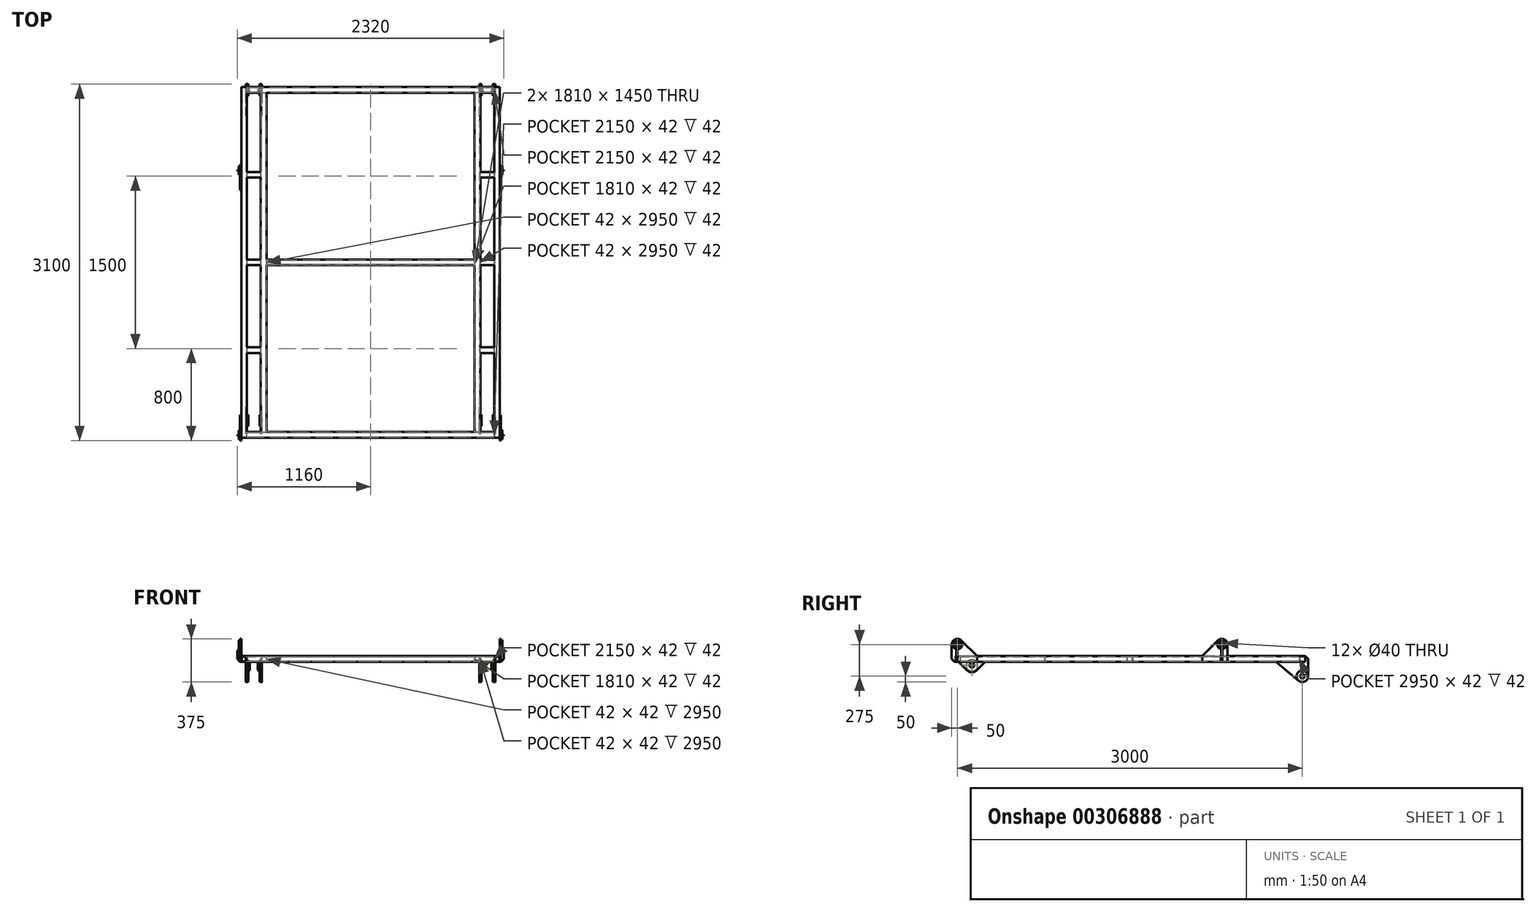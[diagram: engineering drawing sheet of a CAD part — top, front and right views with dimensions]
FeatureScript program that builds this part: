
annotation { "Feature Type Name" : "Feature", "Feature Type Description" : "" }
export const myFeature = defineFeature(function(context is Context, id is Id, definition is map)
    precondition{}
    {
        {
            assignVariable(context, id + "F0", {"name" : "width_centres", "anyValue" : 2200});
        }
        {
            assignVariable(context, id + "F1", {"name" : "offset_centres", "anyValue" : getVariable(context, 'width_centres') / 2});
        }
        {
            assignVariable(context, id + "F2", {"name" : "locater_centre_length", "anyValue" : 2300});
        }
        {
            assignVariable(context, id + "F3", {"name" : "mounting_support_offset", "anyValue" : 170});
        }
        {
            var Q0;
            Q0=qCreatedBy(makeId("Top.planeOp"),FACE);
            var sketch = newSketch(context, id + "F4", { "sketchPlane" : qUnion([Q0])});
            skLineSegment(sketch, "E0", {"start": v(0, 0) * mm, "end": v(-1100, 0) * mm, "construction": true});
            skLineSegment(sketch, "E1", {"start": v(-1100, 0) * mm, "end": v(-1100, -3050) * mm, "construction": true});
            skLineSegment(sketch, "E2", {"start": v(-1100, -3050) * mm, "end": v(0, -3050) * mm, "construction": true});
            skLineSegment(sketch, "E3", {"start": v(-1100, -1525) * mm, "end": v(0, -1525) * mm, "construction": true});
            skLineSegment(sketch, "E4", {"start": v(-930, 0) * mm, "end": v(-930, -3050) * mm, "construction": true});
            skPoint(sketch, "E5", {"position": v(-1100, 0) * mm});
            skPoint(sketch, "E6", {"position": v(-930, 0) * mm});
            skPoint(sketch, "E7", {"position": v(-1100, -1525) * mm});
            skPoint(sketch, "E8", {"position": v(-930, -1525) * mm});
            skPoint(sketch, "E9", {"position": v(-1100, -3050) * mm});
            skPoint(sketch, "E10", {"position": v(-930, -3050) * mm});
            skPoint(sketch, "E11", {"position": v(0, -3050) * mm});
            skPoint(sketch, "E12", {"position": v(0, -1525) * mm});
            skPoint(sketch, "E13", {"position": v(0, 0) * mm});
            skLineSegment(sketch, "E14", {"start": v(-930, -3050) * mm, "end": v(0, -1525) * mm, "construction": true});
            skLineSegment(sketch, "E15", {"start": v(-930, 0) * mm, "end": v(0, -1525) * mm, "construction": true});
            skSolve(sketch);
        }
        {
            var Q0;
            Q0=qCreatedBy(makeId("Front.planeOp"),FACE);
            var Q1;
            Q1=sQuery(id+"F4.wireOp",VERTEX,"E11");
            cPlane(context, id + "F5", {"entities" : qUnion([Q0, Q1]), "cplaneType" : CPlaneType.PLANE_POINT, "offset" : 25 * mm, "width" : 150 * mm, "height" : 150 * mm});
        }
        {
            var Q0;
            Q0=qCreatedBy(id+"F5.planeOp",FACE);
            var sketch = newSketch(context, id + "F6", { "sketchPlane" : qUnion([Q0])});
            skPoint(sketch, "E16", {"position": v(-1203.55, -13.4) * mm});
            skPoint(sketch, "E17", {"position": v(-1303.55, -13.4) * mm});
            skPoint(sketch, "E18", {"position": v(-1003.55, -13.4) * mm});
            skLineSegment(sketch, "E19.bottom", {"start": v(-1125, 25) * mm, "end": v(-1075, 25) * mm});
            skLineSegment(sketch, "E19.top", {"start": v(-1125, -25) * mm, "end": v(-1075, -25) * mm});
            skLineSegment(sketch, "E19.left", {"start": v(-1125, 25) * mm, "end": v(-1125, -25) * mm});
            skLineSegment(sketch, "E19.right", {"start": v(-1075, 25) * mm, "end": v(-1075, -25) * mm});
            skPoint(sketch, "E19.middle", {"position": v(-1100, 0) * mm});
            skLineSegment(sketch, "E20.0", {"start": v(-1121, 21) * mm, "end": v(-1079, 21) * mm});
            skLineSegment(sketch, "E20.1", {"start": v(-1121, 21) * mm, "end": v(-1121, -21) * mm});
            skLineSegment(sketch, "E20.2", {"start": v(-1121, -21) * mm, "end": v(-1079, -21) * mm});
            skLineSegment(sketch, "E20.3", {"start": v(-1079, 21) * mm, "end": v(-1079, -21) * mm});
            skPoint(sketch, "E21", {"position": v(-1125, 25) * mm});
            skPoint(sketch, "E22", {"position": v(-1075, 25) * mm});
            skPoint(sketch, "E23", {"position": v(-1075, -25) * mm});
            skPoint(sketch, "E24", {"position": v(-1125, -25) * mm});
            skSolve(sketch);
        }
        {
            var Q0;
            Q0 = qSketchRegion(id + "F6", true);
            var Q1;
            Q1=sQuery(id+"F4.wireOp",VERTEX,"E5");
            extrude(context, id + "F7", {"entities" : qUnion([Q0]), "endBound" : BoundingType.UP_TO_VERTEX, "oppositeDirection" : true, "endBoundEntityVertex" : qUnion([Q1]), "depth" : 25 * mm});
        }
        {
            var Q0;
            Q0=qCreatedBy(makeId("Right.planeOp"),FACE);
            var sketch = newSketch(context, id + "F8", { "sketchPlane" : qUnion([Q0])});
            skPoint(sketch, "E25", {"position": v(-1835.18, -71.7) * mm});
            skPoint(sketch, "E26", {"position": v(-1935.18, -71.7) * mm});
            skPoint(sketch, "E27", {"position": v(-1635.18, -71.7) * mm});
            skLineSegment(sketch, "E28.bottom", {"start": v(-3050, 25) * mm, "end": v(-3000, 25) * mm});
            skLineSegment(sketch, "E28.top", {"start": v(-3050, -25) * mm, "end": v(-3000, -25) * mm});
            skLineSegment(sketch, "E28.left", {"start": v(-3050, 25) * mm, "end": v(-3050, -25) * mm});
            skLineSegment(sketch, "E28.right", {"start": v(-3000, 25) * mm, "end": v(-3000, -25) * mm});
            skPoint(sketch, "E28.middle", {"position": v(-3025, 0) * mm});
            skLineSegment(sketch, "E29.0", {"start": v(-3046, 21) * mm, "end": v(-3004, 21) * mm});
            skLineSegment(sketch, "E29.1", {"start": v(-3046, 21) * mm, "end": v(-3046, -21) * mm});
            skLineSegment(sketch, "E29.2", {"start": v(-3046, -21) * mm, "end": v(-3004, -21) * mm});
            skLineSegment(sketch, "E29.3", {"start": v(-3004, 21) * mm, "end": v(-3004, -21) * mm});
            skPoint(sketch, "E30", {"position": v(-3050, 25) * mm});
            skPoint(sketch, "E31", {"position": v(-3000, 25) * mm});
            skPoint(sketch, "E32", {"position": v(-3000, -25) * mm});
            skPoint(sketch, "E33", {"position": v(-3050, -25) * mm});
            skPoint(sketch, "E34", {"position": v(-210.58, -52.8) * mm});
            skPoint(sketch, "E35", {"position": v(-310.58, -52.8) * mm});
            skPoint(sketch, "E36", {"position": v(-10.58, -52.8) * mm});
            skLineSegment(sketch, "E37.bottom", {"start": v(-50, 25) * mm, "end": v(0, 25) * mm});
            skLineSegment(sketch, "E37.top", {"start": v(-50, -25) * mm, "end": v(0, -25) * mm});
            skLineSegment(sketch, "E37.left", {"start": v(-50, 25) * mm, "end": v(-50, -25) * mm});
            skLineSegment(sketch, "E37.right", {"start": v(0, 25) * mm, "end": v(0, -25) * mm});
            skPoint(sketch, "E37.middle", {"position": v(-25, 0) * mm});
            skLineSegment(sketch, "E38.0", {"start": v(-46, 21) * mm, "end": v(-4, 21) * mm});
            skLineSegment(sketch, "E38.1", {"start": v(-46, 21) * mm, "end": v(-46, -21) * mm});
            skLineSegment(sketch, "E38.2", {"start": v(-46, -21) * mm, "end": v(-4, -21) * mm});
            skLineSegment(sketch, "E38.3", {"start": v(-4, 21) * mm, "end": v(-4, -21) * mm});
            skPoint(sketch, "E39", {"position": v(-50, 25) * mm});
            skPoint(sketch, "E40", {"position": v(0, 25) * mm});
            skPoint(sketch, "E41", {"position": v(0, -25) * mm});
            skPoint(sketch, "E42", {"position": v(-50, -25) * mm});
            skSolve(sketch);
        }
        {
            var Q0;
            Q0 = qSketchRegion(id + "F8", true);
            var Q1;
            Q1=makeQuery(id+"F7.opExtrude","SWEPT_BODY",BODY,{"disambiguationData":[OSD([sQuery(id+"F6.wireOp",EDGE,"E19.bottom"),sQuery(id+"F6.wireOp",EDGE,"E19.top"),sQuery(id+"F6.wireOp",EDGE,"E19.left"),sQuery(id+"F6.wireOp",EDGE,"E19.right"),sQuery(id+"F6.wireOp",EDGE,"E20.0"),sQuery(id+"F6.wireOp",EDGE,"E20.1"),sQuery(id+"F6.wireOp",EDGE,"E20.2"),sQuery(id+"F6.wireOp",EDGE,"E20.3")])]});
            extrude(context, id + "F9", {"entities" : qUnion([Q0]), "operationType" : NewBodyOperationType.ADD, "endBound" : BoundingType.UP_TO_NEXT, "oppositeDirection" : true, "endBoundEntityBody" : qUnion([Q1]), "depth" : 25 * mm});
        }
        {
            var Q0;
            Q0=qCreatedBy(makeId("Front.planeOp"),FACE);
            var Q1;
            Q1=sQuery(id+"F4.wireOp",VERTEX,"E12");
            cPlane(context, id + "F10", {"entities" : qUnion([Q0, Q1]), "cplaneType" : CPlaneType.PLANE_POINT, "offset" : 25 * mm, "width" : 150 * mm, "height" : 150 * mm});
        }
        {
            var Q0;
            Q0=qCreatedBy(id+"F10.planeOp",FACE);
            var sketch = newSketch(context, id + "F11", { "sketchPlane" : qUnion([Q0])});
            skPoint(sketch, "E43", {"position": v(-1051.26, -74.87) * mm});
            skPoint(sketch, "E44", {"position": v(-1151.26, -74.87) * mm});
            skPoint(sketch, "E45", {"position": v(-851.26, -74.87) * mm});
            skLineSegment(sketch, "E46.bottom", {"start": v(-955, 25) * mm, "end": v(-905, 25) * mm});
            skLineSegment(sketch, "E46.top", {"start": v(-955, -25) * mm, "end": v(-905, -25) * mm});
            skLineSegment(sketch, "E46.left", {"start": v(-955, 25) * mm, "end": v(-955, -25) * mm});
            skLineSegment(sketch, "E46.right", {"start": v(-905, 25) * mm, "end": v(-905, -25) * mm});
            skPoint(sketch, "E46.middle", {"position": v(-930, 0) * mm});
            skLineSegment(sketch, "E47.0", {"start": v(-951, 21) * mm, "end": v(-909, 21) * mm});
            skLineSegment(sketch, "E47.1", {"start": v(-951, 21) * mm, "end": v(-951, -21) * mm});
            skLineSegment(sketch, "E47.2", {"start": v(-951, -21) * mm, "end": v(-909, -21) * mm});
            skLineSegment(sketch, "E47.3", {"start": v(-909, 21) * mm, "end": v(-909, -21) * mm});
            skPoint(sketch, "E48", {"position": v(-955, 25) * mm});
            skPoint(sketch, "E49", {"position": v(-905, 25) * mm});
            skPoint(sketch, "E50", {"position": v(-905, -25) * mm});
            skPoint(sketch, "E51", {"position": v(-955, -25) * mm});
            skSolve(sketch);
        }
        {
            var Q0;
            Q0 = qSketchRegion(id + "F11", true);
            extrude(context, id + "F12", {"entities" : qUnion([Q0]), "operationType" : NewBodyOperationType.ADD, "depth" : (getVariable(context, 'locater_centre_length') + 700 - 50) * mm, "symmetric" : true});
        }
        {
            var Q0;
            Q0=qCreatedBy(makeId("Right.planeOp"),FACE);
            var sketch = newSketch(context, id + "F13", { "sketchPlane" : qUnion([Q0])});
            skPoint(sketch, "E52", {"position": v(-973.87, -66.92) * mm});
            skPoint(sketch, "E53", {"position": v(-1073.87, -66.92) * mm});
            skPoint(sketch, "E54", {"position": v(-773.87, -66.92) * mm});
            skLineSegment(sketch, "E55.bottom", {"start": v(-1550, 25) * mm, "end": v(-1500, 25) * mm});
            skLineSegment(sketch, "E55.top", {"start": v(-1550, -25) * mm, "end": v(-1500, -25) * mm});
            skLineSegment(sketch, "E55.left", {"start": v(-1550, 25) * mm, "end": v(-1550, -25) * mm});
            skLineSegment(sketch, "E55.right", {"start": v(-1500, 25) * mm, "end": v(-1500, -25) * mm});
            skPoint(sketch, "E55.middle", {"position": v(-1525, 0) * mm});
            skLineSegment(sketch, "E56.0", {"start": v(-1546, 21) * mm, "end": v(-1504, 21) * mm});
            skLineSegment(sketch, "E56.1", {"start": v(-1546, 21) * mm, "end": v(-1546, -21) * mm});
            skLineSegment(sketch, "E56.2", {"start": v(-1546, -21) * mm, "end": v(-1504, -21) * mm});
            skLineSegment(sketch, "E56.3", {"start": v(-1504, 21) * mm, "end": v(-1504, -21) * mm});
            skPoint(sketch, "E57", {"position": v(-1550, 25) * mm});
            skPoint(sketch, "E58", {"position": v(-1500, 25) * mm});
            skPoint(sketch, "E59", {"position": v(-1500, -25) * mm});
            skPoint(sketch, "E60", {"position": v(-1550, -25) * mm});
            skSolve(sketch);
        }
        {
            var Q0;
            Q0 = qSketchRegion(id + "F13", true);
            var Q1;
            Q1=makeQuery(id+"F7.opExtrude","SWEPT_BODY",BODY,{"disambiguationData":[OSD([sQuery(id+"F6.wireOp",EDGE,"E19.bottom"),sQuery(id+"F6.wireOp",EDGE,"E19.top"),sQuery(id+"F6.wireOp",EDGE,"E19.left"),sQuery(id+"F6.wireOp",EDGE,"E19.right"),sQuery(id+"F6.wireOp",EDGE,"E20.0"),sQuery(id+"F6.wireOp",EDGE,"E20.1"),sQuery(id+"F6.wireOp",EDGE,"E20.2"),sQuery(id+"F6.wireOp",EDGE,"E20.3")])]});
            extrude(context, id + "F14", {"entities" : qUnion([Q0]), "operationType" : NewBodyOperationType.ADD, "endBound" : BoundingType.UP_TO_BODY, "oppositeDirection" : true, "endBoundEntityBody" : qUnion([Q1]), "depth" : 25 * mm});
        }
        {
            var Q0;
            Q0=qCreatedBy(makeId("Right.planeOp"),FACE);
            cPlane(context, id + "F15", {"entities" : qUnion([Q0]), "cplaneType" : CPlaneType.OFFSET, "offset" : (getVariable(context, 'offset_centres') + 25) * mm, "oppositeDirection" : true, "width" : 150 * mm, "height" : 150 * mm});
        }
        {
            var Q0;
            Q0=qCreatedBy(id+"F15.planeOp",FACE);
            var sketch = newSketch(context, id + "F16", { "sketchPlane" : qUnion([Q0])});
            skPoint(sketch, "E61.0", {"position": v(-3050, -25) * mm});
            skPoint(sketch, "E62", {"position": v(-3025, 125) * mm});
            skArc(sketch, "E63", {"start": v(-2989.64, 160.36) * mm, "mid": v(-3044.13, 171.2) * mm, "end": v(-3075, 125) * mm});
            skLineSegment(sketch, "E64", {"start": v(-3050, -25) * mm, "end": v(-3075, 0) * mm});
            skLineSegment(sketch, "E65", {"start": v(-3075, 125) * mm, "end": v(-3075, 0) * mm});
            skPoint(sketch, "E66.0", {"position": v(-3050, 25) * mm});
            skLineSegment(sketch, "E67.0", {"start": v(-2854.29, 25) * mm, "end": v(-1550, 25) * mm, "construction": true});
            skLineSegment(sketch, "E68", {"start": v(-2989.64, 160.36) * mm, "end": v(-2854.29, 25) * mm});
            skCircle(sketch, "E69", {"center": v(-3025, 125) * mm, "radius": 20 * mm});
            skLineSegment(sketch, "E70", {"start": v(-2854.29, 25) * mm, "end": v(-2854.29, -25) * mm});
            skLineSegment(sketch, "E71", {"start": v(-2854.29, -25) * mm, "end": v(-3050, -25) * mm});
            skPoint(sketch, "E72.orphan", {"position": v(-3000, 25) * mm});
            skSolve(sketch);
        }
        {
            var Q0;
            Q0 = qSketchRegion(id + "F16", true);
            extrude(context, id + "F17", {"entities" : qUnion([Q0]), "operationType" : NewBodyOperationType.ADD, "oppositeDirection" : true, "depth" : 10 * mm});
        }
        {
            var Q0;
            Q0=qCreatedBy(id+"F15.planeOp",FACE);
            var sketch = newSketch(context, id + "F18", { "sketchPlane" : qUnion([Q0])});
            skCircle(sketch, "E73", {"center": v(-725, 125) * mm, "radius": 20 * mm});
            skArc(sketch, "E74", {"start": v(-689.64, 160.36) * mm, "mid": v(-725, 175) * mm, "end": v(-760.36, 160.36) * mm});
            skLineSegment(sketch, "E75.0", {"start": v(-1500, 25) * mm, "end": v(-895.71, 25) * mm, "construction": true});
            skLineSegment(sketch, "E76", {"start": v(-895.71, 25) * mm, "end": v(-675, 25) * mm});
            skLineSegment(sketch, "E77", {"start": v(-895.71, 25) * mm, "end": v(-760.36, 160.36) * mm});
            skLineSegment(sketch, "E78.0", {"start": v(-1500, -25) * mm, "end": v(-675, -25) * mm, "construction": true});
            skLineSegment(sketch, "E79", {"start": v(-895.71, 25) * mm, "end": v(-895.71, -25) * mm});
            skLineSegment(sketch, "E80", {"start": v(-895.71, -25) * mm, "end": v(-675, -25) * mm});
            skLineSegment(sketch, "E81.trimOffspring", {"start": v(-282.87, 25) * mm, "end": v(-50, 25) * mm, "construction": true});
            skArc(sketch, "E82", {"start": v(-689.64, 160.36) * mm, "mid": v(-678.8, 144.13) * mm, "end": v(-675, 125) * mm});
            skLineSegment(sketch, "E83", {"start": v(-675, 125) * mm, "end": v(-675, -25) * mm});
            skPoint(sketch, "E84.orphan", {"position": v(-689.64, 89.64) * mm});
            skLineSegment(sketch, "E85.trimOffspring", {"start": v(-282.87, -25) * mm, "end": v(-50, -25) * mm, "construction": true});
            skCircle(sketch, "E86.0", {"center": v(-3025, 125) * mm, "radius": 20 * mm, "construction": true});
            skSolve(sketch);
        }
        {
            var Q0;
            Q0 = qSketchRegion(id + "F18", true);
            extrude(context, id + "F19", {"entities" : qUnion([Q0]), "operationType" : NewBodyOperationType.ADD, "oppositeDirection" : true, "depth" : 10 * mm});
        }
        {
            var Q0;
            Q0=qCreatedBy(id+"F15.planeOp",FACE);
            cPlane(context, id + "F20", {"entities" : qUnion([Q0]), "cplaneType" : CPlaneType.OFFSET, "offset" : 50 * mm, "width" : 150 * mm, "height" : 150 * mm});
        }
        {
            var Q0;
            Q0=qCreatedBy(id+"F20.planeOp",FACE);
            var sketch = newSketch(context, id + "F21", { "sketchPlane" : qUnion([Q0])});
            skPoint(sketch, "E87", {"position": v(-25, -150) * mm});
            skCircle(sketch, "E88", {"center": v(-25, -150) * mm, "radius": 20 * mm});
            skArc(sketch, "E89", {"start": v(-56.96, -188.45) * mm, "mid": v(-3.77, -195.27) * mm, "end": v(25, -150) * mm});
            skLineSegment(sketch, "E90.0", {"start": v(-1500, -25) * mm, "end": v(-50, -25) * mm, "construction": true});
            skPoint(sketch, "E91.0", {"position": v(0, -25) * mm});
            skPoint(sketch, "E92.0", {"position": v(0, 25) * mm});
            skLineSegment(sketch, "E93", {"start": v(0, 25) * mm, "end": v(25, 0) * mm});
            skLineSegment(sketch, "E94", {"start": v(25, -150) * mm, "end": v(25, 0) * mm});
            skLineSegment(sketch, "E95", {"start": v(-56.96, -188.45) * mm, "end": v(-253.57, -25) * mm});
            skLineSegment(sketch, "E96", {"start": v(-253.57, -25) * mm, "end": v(0, -25) * mm});
            skLineSegment(sketch, "E97", {"start": v(0, 25) * mm, "end": v(0, -25) * mm});
            skPoint(sketch, "E98.end.orphan", {"position": v(-253.57, 25) * mm});
            skSolve(sketch);
        }
        {
            var Q0;
            Q0 = qSketchRegion(id + "F21", true);
            extrude(context, id + "F22", {"entities" : qUnion([Q0]), "operationType" : NewBodyOperationType.ADD, "oppositeDirection" : true, "depth" : 10 * mm});
        }
        {
            var Q0;
            Q0=qCreatedBy(id+"F20.planeOp",FACE);
            var sketch = newSketch(context, id + "F23", { "sketchPlane" : qUnion([Q0])});
            skPoint(sketch, "E99", {"position": v(-2900, -55) * mm});
            skPoint(sketch, "E100.0", {"position": v(-3050, -25) * mm});
            skLineSegment(sketch, "E101.0", {"start": v(-3000, 25) * mm, "end": v(-1550, 25) * mm, "construction": true});
            skLineSegment(sketch, "E102.0", {"start": v(-3000, -25) * mm, "end": v(-1550, -25) * mm, "construction": true});
            skPoint(sketch, "E103.0", {"position": v(-3000, 0) * mm});
            skCircle(sketch, "E104", {"center": v(-2900, -55) * mm, "radius": 20 * mm});
            skArc(sketch, "E105", {"start": v(-2942.43, -97.43) * mm, "mid": v(-2900, -115) * mm, "end": v(-2857.57, -97.43) * mm});
            skLineSegment(sketch, "E106", {"start": v(-2942.43, -97.43) * mm, "end": v(-3014.85, -25) * mm});
            skLineSegment(sketch, "E107", {"start": v(-2857.57, -97.43) * mm, "end": v(-2785.15, -25) * mm});
            skLineSegment(sketch, "E108", {"start": v(-3000, -25) * mm, "end": v(-2785.15, -25) * mm});
            skLineSegment(sketch, "E109", {"start": v(-3014.85, -25) * mm, "end": v(-3000, -25) * mm});
            skSolve(sketch);
        }
        {
            var Q0;
            Q0 = qSketchRegion(id + "F23", true);
            extrude(context, id + "F24", {"entities" : qUnion([Q0]), "operationType" : NewBodyOperationType.ADD, "oppositeDirection" : true, "depth" : 10 * mm});
        }
        {
            var Q0;
            Q0=qCreatedBy(id+"F20.planeOp",FACE);
            cPlane(context, id + "F25", {"entities" : qUnion([Q0]), "cplaneType" : CPlaneType.OFFSET, "offset" : (getVariable(context, 'mounting_support_offset') - 50) * mm, "width" : 150 * mm, "height" : 150 * mm});
        }
        {
            var Q0;
            Q0=qCreatedBy(id+"F25.planeOp",FACE);
            var sketch = newSketch(context, id + "F26", { "sketchPlane" : qUnion([Q0])});
            skLineSegment(sketch, "E110.0", {"start": v(-56.96, -188.45) * mm, "end": v(-253.57, -25) * mm});
            skPoint(sketch, "E111.0", {"position": v(-3.77, -195.27) * mm});
            skArc(sketch, "E112.0", {"start": v(-56.96, -188.45) * mm, "mid": v(-3.77, -195.27) * mm, "end": v(25, -150) * mm});
            skLineSegment(sketch, "E113.0", {"start": v(25, -150) * mm, "end": v(25, 0) * mm});
            skLineSegment(sketch, "E114.0", {"start": v(0, 25) * mm, "end": v(25, 0) * mm});
            skPoint(sketch, "E115.0", {"position": v(0, -25) * mm});
            skLineSegment(sketch, "E116", {"start": v(-253.57, -25) * mm, "end": v(0, -25) * mm});
            skLineSegment(sketch, "E117", {"start": v(0, -25) * mm, "end": v(0, 25) * mm});
            skCircle(sketch, "E118.0", {"center": v(-25, -150) * mm, "radius": 20 * mm});
            skCircle(sketch, "E119.0", {"center": v(-2900, -55) * mm, "radius": 20 * mm});
            skLineSegment(sketch, "E120.0", {"start": v(-2857.57, -97.43) * mm, "end": v(-2785.15, -25) * mm});
            skArc(sketch, "E121.0", {"start": v(-2942.43, -97.43) * mm, "mid": v(-2900, -115) * mm, "end": v(-2857.57, -97.43) * mm});
            skLineSegment(sketch, "E122.0", {"start": v(-2942.43, -97.43) * mm, "end": v(-3014.85, -25) * mm});
            skLineSegment(sketch, "E123", {"start": v(-3014.85, -25) * mm, "end": v(-2785.15, -25) * mm});
            skSolve(sketch);
        }
        {
            var Q0;
            Q0 = qSketchRegion(id + "F26", true);
            extrude(context, id + "F27", {"entities" : qUnion([Q0]), "operationType" : NewBodyOperationType.ADD, "depth" : 10 * mm});
        }
        {
            var Q0;
            Q0=qCreatedBy(id+"F15.planeOp",FACE);
            cPlane(context, id + "F28", {"entities" : qUnion([Q0]), "cplaneType" : CPlaneType.OFFSET, "offset" : 10 * mm, "oppositeDirection" : true, "width" : 150 * mm, "height" : 150 * mm});
        }
        {
            var Q0;
            Q0=qCreatedBy(id+"F28.planeOp",FACE);
            var sketch = newSketch(context, id + "F29", { "sketchPlane" : qUnion([Q0])});
            skCircle(sketch, "E124.0", {"center": v(-725, 125) * mm, "radius": 20 * mm});
            skCircle(sketch, "E125", {"center": v(-725, 125) * mm, "radius": 40 * mm});
            skCircle(sketch, "E126.0", {"center": v(-3025, 125) * mm, "radius": 20 * mm});
            skCircle(sketch, "E127", {"center": v(-3025, 125) * mm, "radius": 40 * mm});
            skSolve(sketch);
        }
        {
            var Q0;
            Q0 = qSketchRegion(id + "F29", true);
            extrude(context, id + "F30", {"entities" : qUnion([Q0]), "operationType" : NewBodyOperationType.ADD, "oppositeDirection" : true, "depth" : 10 * mm});
        }
        {
            var Q0;
            Q0=qCreatedBy(id+"F20.planeOp",FACE);
            var sketch = newSketch(context, id + "F31", { "sketchPlane" : qUnion([Q0])});
            skCircle(sketch, "E128.0", {"center": v(-2900, -55) * mm, "radius": 20 * mm});
            skCircle(sketch, "E129", {"center": v(-2900, -55) * mm, "radius": 50 * mm});
            skCircle(sketch, "E130.0", {"center": v(-25, -150) * mm, "radius": 20 * mm});
            skCircle(sketch, "E131", {"center": v(-25, -150) * mm, "radius": 50 * mm});
            skSolve(sketch);
        }
        {
            var Q0;
            Q0 = qSketchRegion(id + "F31", true);
            extrude(context, id + "F32", {"entities" : qUnion([Q0]), "operationType" : NewBodyOperationType.ADD, "depth" : 10 * mm});
        }
        {
            var Q0;
            Q0=qCreatedBy(id+"F25.planeOp",FACE);
            var sketch = newSketch(context, id + "F33", { "sketchPlane" : qUnion([Q0])});
            skCircle(sketch, "E132.0", {"center": v(-2900, -55) * mm, "radius": 50 * mm});
            skCircle(sketch, "E133.0", {"center": v(-2900, -55) * mm, "radius": 20 * mm});
            skCircle(sketch, "E134.0.0", {"center": v(-25, -150) * mm, "radius": 50 * mm});
            skCircle(sketch, "E135.0", {"center": v(-25, -150) * mm, "radius": 20 * mm});
            skSolve(sketch);
        }
        {
            var Q0;
            Q0 = qSketchRegion(id + "F33", true);
            extrude(context, id + "F34", {"entities" : qUnion([Q0]), "operationType" : NewBodyOperationType.ADD, "oppositeDirection" : true, "depth" : 10 * mm});
        }
        {
            var Q0;
            Q0=qCreatedBy(id+"F5.planeOp",FACE);
            cPlane(context, id + "F35", {"entities" : qUnion([Q0]), "cplaneType" : CPlaneType.OFFSET, "offset" : 25 * mm, "oppositeDirection" : true, "width" : 150 * mm, "height" : 150 * mm});
        }
        {
            var Q0;
            Q0=qCreatedBy(id+"F35.planeOp",FACE);
            var sketch = newSketch(context, id + "F36", { "sketchPlane" : qUnion([Q0])});
            skPoint(sketch, "E136.0", {"position": v(-1135, -25) * mm});
            skLineSegment(sketch, "E137", {"start": v(-1135, -25) * mm, "end": v(-1135, 84.9) * mm});
            skLineSegment(sketch, "E138", {"start": v(-1145, 84.9) * mm, "end": v(-1160, 69.9) * mm});
            skLineSegment(sketch, "E139", {"start": v(-1160, 69.9) * mm, "end": v(-1160, 0) * mm});
            skLineSegment(sketch, "E140", {"start": v(-1160, 0) * mm, "end": v(-1135, -25) * mm});
            skLineSegment(sketch, "E141", {"start": v(-1145, 84.9) * mm, "end": v(-1135, 84.9) * mm});
            skPoint(sketch, "E142.orphan", {"position": v(-1135, 85) * mm});
            skSolve(sketch);
        }
        {
            var Q0;
            Q0 = qSketchRegion(id + "F36", true);
            extrude(context, id + "F37", {"entities" : qUnion([Q0]), "operationType" : NewBodyOperationType.ADD, "depth" : 10 * mm});
        }
        {
            var Q0;
            Q0=qCreatedBy(id+"F35.planeOp",FACE);
            cPlane(context, id + "F38", {"entities" : qUnion([Q0]), "cplaneType" : CPlaneType.OFFSET, "offset" : (getVariable(context, 'locater_centre_length')) * mm, "oppositeDirection" : true, "width" : 150 * mm, "height" : 150 * mm});
        }
        {
            var Q0;
            Q0=qCreatedBy(id+"F38.planeOp",FACE);
            var sketch = newSketch(context, id + "F39", { "sketchPlane" : qUnion([Q0])});
            skLineSegment(sketch, "E143.0.0", {"start": v(-1160, 69.9) * mm, "end": v(-1145, 84.9) * mm});
            skLineSegment(sketch, "E143.0.1", {"start": v(-1145, 84.9) * mm, "end": v(-1135, 84.9) * mm});
            skLineSegment(sketch, "E143.0.2", {"start": v(-1135, 84.9) * mm, "end": v(-1135, -25) * mm});
            skLineSegment(sketch, "E143.0.3", {"start": v(-1135, -25) * mm, "end": v(-1160, 0) * mm});
            skLineSegment(sketch, "E143.0.4", {"start": v(-1160, 0) * mm, "end": v(-1160, 69.9) * mm});
            skSolve(sketch);
        }
        {
            var Q0;
            Q0 = qSketchRegion(id + "F39", true);
            extrude(context, id + "F40", {"entities" : qUnion([Q0]), "operationType" : NewBodyOperationType.ADD, "depth" : 10 * mm, "symmetric" : true});
        }
        {
            var Q0;
            Q0=qCreatedBy(makeId("Front.planeOp"),FACE);
            cPlane(context, id + "F41", {"entities" : qUnion([Q0]), "cplaneType" : CPlaneType.OFFSET, "offset" : 25 * mm, "width" : 150 * mm, "height" : 150 * mm});
        }
        {
            var Q0;
            Q0=qCreatedBy(id+"F41.planeOp",FACE);
            var sketch = newSketch(context, id + "F42", { "sketchPlane" : qUnion([Q0])});
            skLineSegment(sketch, "E144.0", {"start": v(-1075, -25) * mm, "end": v(-955, -25) * mm, "construction": true});
            skLineSegment(sketch, "E145", {"start": v(-955, -109.9) * mm, "end": v(-955, -25) * mm});
            skLineSegment(sketch, "E146", {"start": v(-955, -25) * mm, "end": v(-980, -25) * mm});
            skLineSegment(sketch, "E147", {"start": v(-980, -25) * mm, "end": v(-980, -95) * mm});
            skLineSegment(sketch, "E148", {"start": v(-980, -95) * mm, "end": v(-965.1, -109.9) * mm});
            skLineSegment(sketch, "E149", {"start": v(-1075, -109.9) * mm, "end": v(-1075, -25) * mm});
            skLineSegment(sketch, "E150", {"start": v(-1075, -25) * mm, "end": v(-1050, -25) * mm});
            skLineSegment(sketch, "E151", {"start": v(-1050, -25) * mm, "end": v(-1050, -95) * mm});
            skLineSegment(sketch, "E152", {"start": v(-1050, -95) * mm, "end": v(-1064.9, -109.9) * mm});
            skLineSegment(sketch, "E153", {"start": v(-955, -109.9) * mm, "end": v(-965.1, -109.9) * mm});
            skLineSegment(sketch, "E154", {"start": v(-1064.9, -109.9) * mm, "end": v(-1075, -109.9) * mm});
            skSolve(sketch);
        }
        {
            var Q0;
            Q0 = qSketchRegion(id + "F42", true);
            extrude(context, id + "F43", {"entities" : qUnion([Q0]), "operationType" : NewBodyOperationType.ADD, "depth" : 10 * mm, "symmetric" : true});
        }
        {
            var Q0;
            Q0=qCreatedBy(makeId("Right.planeOp"),FACE);
            var sketch = newSketch(context, id + "F44", { "sketchPlane" : qUnion([Q0])});
            skCircle(sketch, "E155.0", {"center": v(-3025, 125) * mm, "radius": 20 * mm, "construction": true});
            skCircle(sketch, "E156.0", {"center": v(-2900, -55) * mm, "radius": 20 * mm, "construction": true});
            skCircle(sketch, "E157.0", {"center": v(-725, 125) * mm, "radius": 20 * mm, "construction": true});
            skCircle(sketch, "E158.0", {"center": v(-25, -150) * mm, "radius": 20 * mm, "construction": true});
            skLineSegment(sketch, "E159", {"start": v(-3025, 125) * mm, "end": v(-725, 125) * mm, "construction": true});
            skLineSegment(sketch, "E160", {"start": v(-2900, -55) * mm, "end": v(-2900, 125) * mm, "construction": true});
            skLineSegment(sketch, "E161", {"start": v(-725, 125) * mm, "end": v(-725, 0) * mm, "construction": true});
            skLineSegment(sketch, "E162", {"start": v(-25, -150) * mm, "end": v(-25, 0) * mm, "construction": true});
            skPoint(sketch, "E163.0", {"position": v(-3025, -21) * mm});
            skPoint(sketch, "E164.0", {"position": v(-3050, 0) * mm});
            skPoint(sketch, "E165", {"position": v(-3025, 0) * mm});
            skPoint(sketch, "E166", {"position": v(-25, 0) * mm});
            skSolve(sketch);
        }
        {
            var Q0;
            Q0=qCreatedBy(id+"F25.planeOp",FACE);
            var sketch = newSketch(context, id + "F45", { "sketchPlane" : qUnion([Q0])});
            skPoint(sketch, "E167.0", {"position": v(-1525, 0) * mm});
            skLineSegment(sketch, "E168.0", {"start": v(-725, 125) * mm, "end": v(-725, 0) * mm, "construction": true});
            skPoint(sketch, "E169.0", {"position": v(-2287.5, 0) * mm});
            skPoint(sketch, "E170.0", {"position": v(-762.5, 0) * mm});
            skLineSegment(sketch, "E171.bottom", {"start": v(-2312.5, 25) * mm, "end": v(-2262.5, 25) * mm});
            skLineSegment(sketch, "E171.top", {"start": v(-2266.5, -25) * mm, "end": v(-2262.5, -25) * mm});
            skLineSegment(sketch, "E171.left", {"start": v(-2312.5, 25) * mm, "end": v(-2312.5, 21) * mm});
            skLineSegment(sketch, "E171.right", {"start": v(-2262.5, 25) * mm, "end": v(-2262.5, -25) * mm});
            skLineSegment(sketch, "E172.0", {"start": v(-2266.5, 21) * mm, "end": v(-2266.5, -25) * mm});
            skLineSegment(sketch, "E172.1", {"start": v(-2312.5, 21) * mm, "end": v(-2266.5, 21) * mm});
            skPoint(sketch, "E173.orphan", {"position": v(-2312.5, -25) * mm});
            skPoint(sketch, "E174", {"position": v(-2262.5, 25) * mm});
            skPoint(sketch, "E175", {"position": v(-2312.5, 25) * mm});
            skPoint(sketch, "E176", {"position": v(-2262.5, -25) * mm});
            skLineSegment(sketch, "E177.bottom", {"start": v(-1550, 25) * mm, "end": v(-1500, 25) * mm});
            skLineSegment(sketch, "E177.top", {"start": v(-1504, -25) * mm, "end": v(-1500, -25) * mm});
            skLineSegment(sketch, "E177.left", {"start": v(-1550, 25) * mm, "end": v(-1550, 21) * mm});
            skLineSegment(sketch, "E177.right", {"start": v(-1500, 25) * mm, "end": v(-1500, -25) * mm});
            skLineSegment(sketch, "E178.0", {"start": v(-1504, 21) * mm, "end": v(-1504, -25) * mm});
            skLineSegment(sketch, "E178.1", {"start": v(-1550, 21) * mm, "end": v(-1504, 21) * mm});
            skPoint(sketch, "E179.orphan", {"position": v(-1550, -25) * mm});
            skPoint(sketch, "E180", {"position": v(-1500, 25) * mm});
            skPoint(sketch, "E181", {"position": v(-1550, 25) * mm});
            skPoint(sketch, "E182", {"position": v(-1500, -25) * mm});
            skLineSegment(sketch, "E183.bottom", {"start": v(-787.5, 25) * mm, "end": v(-737.5, 25) * mm});
            skLineSegment(sketch, "E183.top", {"start": v(-741.5, -25) * mm, "end": v(-737.5, -25) * mm});
            skLineSegment(sketch, "E183.left", {"start": v(-787.5, 25) * mm, "end": v(-787.5, 21) * mm});
            skLineSegment(sketch, "E183.right", {"start": v(-737.5, 25) * mm, "end": v(-737.5, -25) * mm});
            skLineSegment(sketch, "E184.0", {"start": v(-741.5, 21) * mm, "end": v(-741.5, -25) * mm});
            skLineSegment(sketch, "E184.1", {"start": v(-787.5, 21) * mm, "end": v(-741.5, 21) * mm});
            skPoint(sketch, "E185.orphan", {"position": v(-787.5, -25) * mm});
            skPoint(sketch, "E186", {"position": v(-737.5, 25) * mm});
            skPoint(sketch, "E187", {"position": v(-787.5, 25) * mm});
            skPoint(sketch, "E188", {"position": v(-737.5, -25) * mm});
            skSolve(sketch);
        }
        {
            var Q0;
            Q0 = qSketchRegion(id + "F45", true);
            var Q1;
            Q1=makeQuery(id+"F24.boolean.opBoolean","MERGE",FACE,{"derivedFrom":[makeQuery(id+"F22.boolean.opBoolean","MERGE",FACE,{"derivedFrom":[makeQuery(id+"F9.boolean.opBoolean","SPLIT",FACE,{"disambiguationData":[TD([makeQuery(id+"F7.opExtrude","SWEPT_FACE",FACE,{"disambiguationData":[OSD([sQuery(id+"F6.wireOp",EDGE,"E19.bottom")])]})])],"derivedFrom":makeQuery(id+"F7.opExtrude","SWEPT_FACE",FACE,{"disambiguationData":[OSD([sQuery(id+"F6.wireOp",EDGE,"E19.right")])]})}),makeQuery(id+"F22.opExtrude","CAP_FACE",FACE,{"disambiguationData":[OSD([sQuery(id+"F21.wireOp",EDGE,"E88"),sQuery(id+"F21.wireOp",EDGE,"E89"),sQuery(id+"F21.wireOp",EDGE,"E93"),sQuery(id+"F21.wireOp",EDGE,"E94"),sQuery(id+"F21.wireOp",EDGE,"E95"),sQuery(id+"F21.wireOp",EDGE,"E96"),sQuery(id+"F21.wireOp",EDGE,"E97")])],"isStart":true})]}),makeQuery(id+"F24.opExtrude","CAP_FACE",FACE,{"disambiguationData":[OSD([sQuery(id+"F23.wireOp",EDGE,"E104"),sQuery(id+"F23.wireOp",EDGE,"E105"),sQuery(id+"F23.wireOp",EDGE,"E106"),sQuery(id+"F23.wireOp",EDGE,"E107"),sQuery(id+"F23.wireOp",EDGE,"E108"),sQuery(id+"F23.wireOp",EDGE,"E109")])],"isStart":true})]});
            extrude(context, id + "F46", {"entities" : qUnion([Q0]), "operationType" : NewBodyOperationType.ADD, "endBound" : BoundingType.UP_TO_SURFACE, "oppositeDirection" : true, "endBoundEntityFace" : qUnion([Q1]), "depth" : 25 * mm});
        }
        {
            var Q0;
            Q0=makeQuery(id+"F7.opExtrude","SWEPT_BODY",BODY,{"disambiguationData":[OSD([sQuery(id+"F6.wireOp",EDGE,"E19.bottom"),sQuery(id+"F6.wireOp",EDGE,"E19.top"),sQuery(id+"F6.wireOp",EDGE,"E19.left"),sQuery(id+"F6.wireOp",EDGE,"E19.right"),sQuery(id+"F6.wireOp",EDGE,"E20.0"),sQuery(id+"F6.wireOp",EDGE,"E20.1"),sQuery(id+"F6.wireOp",EDGE,"E20.2"),sQuery(id+"F6.wireOp",EDGE,"E20.3")])]});
            var Q1;
            Q1=qCreatedBy(makeId("Right.planeOp"),FACE);
            mirror(context, id + "F47", {"operationType" : NewBodyOperationType.ADD, "entities" : qUnion([Q0]), "mirrorPlane" : qUnion([Q1])});
        }
    });
